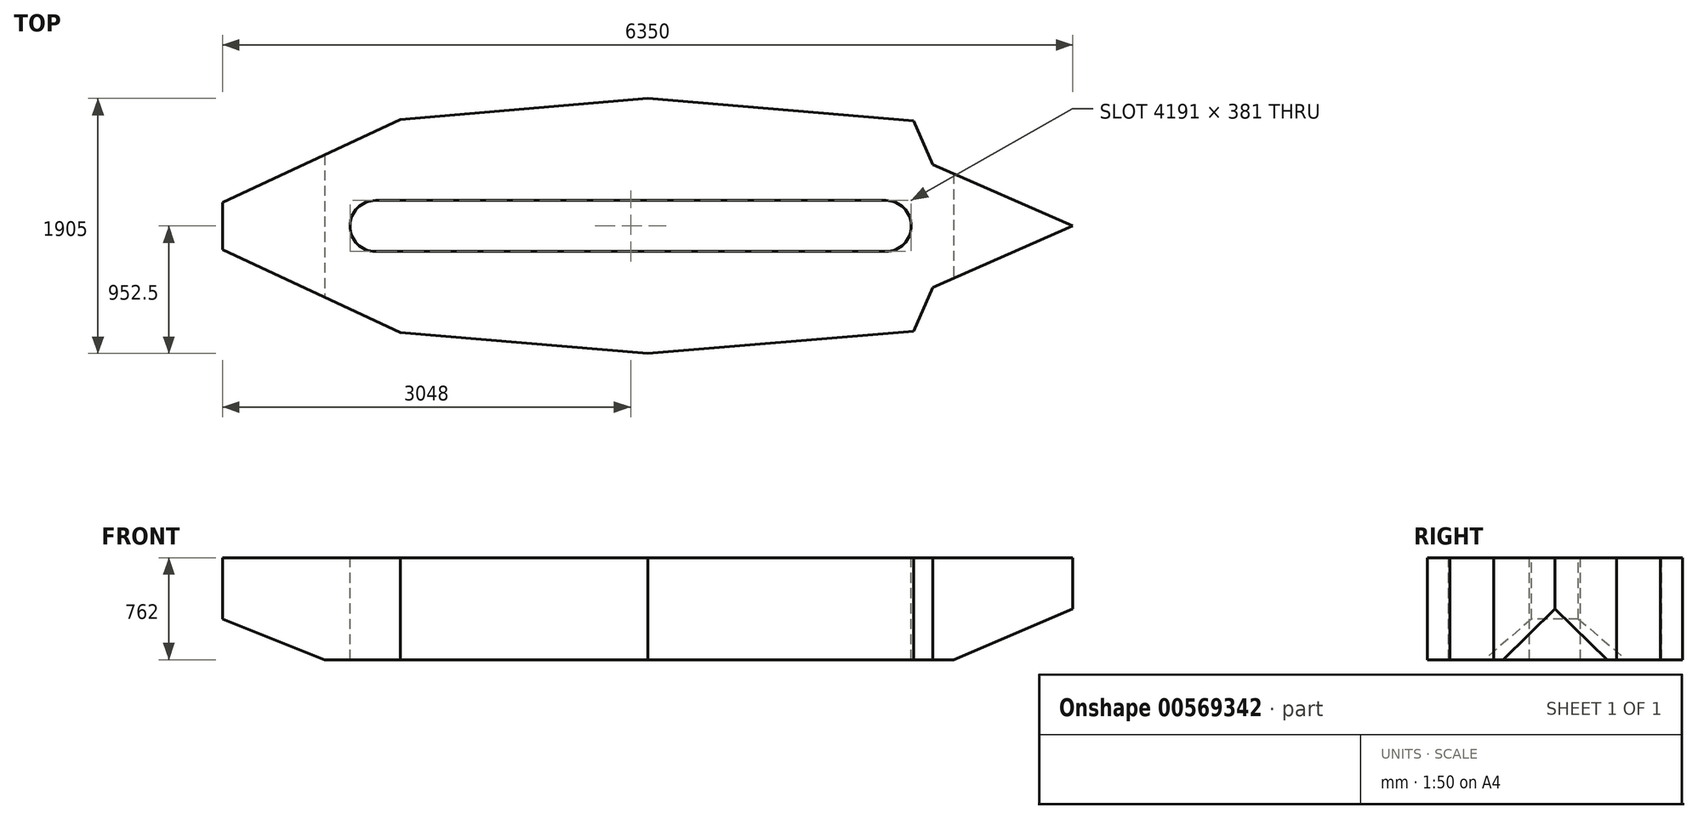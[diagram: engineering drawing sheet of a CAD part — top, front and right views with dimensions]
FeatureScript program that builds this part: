
annotation { "Feature Type Name" : "Feature", "Feature Type Description" : "" }
export const myFeature = defineFeature(function(context is Context, id is Id, definition is map)
    precondition{}
    {
        {
            var Q0;
            Q0=qCreatedBy(makeId("Top.planeOp"),FACE);
            var sketch = newSketch(context, id + "F0", { "sketchPlane" : qUnion([Q0])});
            skLineSegment(sketch, "E0", {"start": v(3175, 0) * mm, "end": v(-3175, 0) * mm, "construction": true});
            skLineSegment(sketch, "E1", {"start": v(0, 952.5) * mm, "end": v(0, -952.5) * mm, "construction": true});
            skLineSegment(sketch, "E2", {"start": v(3175, 0) * mm, "end": v(2128.05, 458.64) * mm});
            skLineSegment(sketch, "E3", {"start": v(2128.05, 458.64) * mm, "end": v(1985.12, 786.19) * mm});
            skLineSegment(sketch, "E4", {"start": v(1985.12, 786.19) * mm, "end": v(0, 952.5) * mm});
            skLineSegment(sketch, "E5", {"start": v(0, 952.5) * mm, "end": v(-1846.34, 794.7) * mm});
            skLineSegment(sketch, "E6", {"start": v(-1846.34, 794.7) * mm, "end": v(-3175, 175.2) * mm});
            skLineSegment(sketch, "E7", {"start": v(-3175, 175.2) * mm, "end": v(-3175, 0) * mm});
            skArc(sketch, "E8", {"start": v(-2032, 190.5) * mm, "mid": v(-2166.7, 134.7) * mm, "end": v(-2222.5, 0) * mm});
            skArc(sketch, "E9", {"start": v(1968.5, 0) * mm, "mid": v(1912.7, 134.7) * mm, "end": v(1778, 190.5) * mm});
            skLineSegment(sketch, "E10", {"start": v(-2032, 190.5) * mm, "end": v(1778, 190.5) * mm});
            skLineSegment(sketch, "E11", {"start": v(-2222.5, 0) * mm, "end": v(-3175, 0) * mm});
            skLineSegment(sketch, "E12", {"start": v(1968.5, 0) * mm, "end": v(3175, 0) * mm});
            skSolve(sketch);
        }
        {
            var Q0;
            Q0=makeQuery(id+"F0.imprint","IMPRINT",FACE,{"disambiguationData":[TD([[makeQuery(id+"F0.imprint","IMPRINT",EDGE,{"derivedFrom":sQuery(id+"F0.wireOp",EDGE,"E2")}),1.0]])]});
            extrude(context, id + "F1", {"entities" : qUnion([Q0]), "oppositeDirection" : true, "depth" : 762 * mm, "offsetDistance" : 25.4 * mm});
        }
        {
            var Q0;
            Q0=makeQuery(id+"F1.opExtrude","SWEPT_FACE",FACE,{"disambiguationData":[OSD([sQuery(id+"F0.wireOp",EDGE,"E11")])]});
            var sketch = newSketch(context, id + "F2", { "sketchPlane" : qUnion([Q0])});
            skLineSegment(sketch, "E13", {"start": v(3175, -381) * mm, "end": v(2286, -762) * mm});
            skLineSegment(sketch, "E14", {"start": v(2286, -762) * mm, "end": v(-2413, -762) * mm});
            skLineSegment(sketch, "E15", {"start": v(-2413, -762) * mm, "end": v(-3175, -457.2) * mm});
            skLineSegment(sketch, "E16", {"start": v(-3175, -457.2) * mm, "end": v(-3175, 0) * mm});
            skLineSegment(sketch, "E17", {"start": v(-3175, 0) * mm, "end": v(3175, 0) * mm});
            skLineSegment(sketch, "E18", {"start": v(3175, 0) * mm, "end": v(3175, -381) * mm});
            skSolve(sketch);
        }
        {
            var Q0;
            Q0 = qSketchRegion(id + "F2", true);
            extrude(context, id + "F3", {"entities" : qUnion([Q0]), "operationType" : NewBodyOperationType.INTERSECT, "endBound" : BoundingType.THROUGH_ALL, "oppositeDirection" : true, "depth" : 25.4 * mm, "offsetDistance" : 25.4 * mm});
        }
        {
            var Q0;
            Q0=makeQuery(id+"F1.opExtrude","SWEPT_BODY",BODY,{"disambiguationData":[OSD([sQuery(id+"F0.wireOp",EDGE,"E2"),sQuery(id+"F0.wireOp",EDGE,"E3"),sQuery(id+"F0.wireOp",EDGE,"E4"),sQuery(id+"F0.wireOp",EDGE,"E5"),sQuery(id+"F0.wireOp",EDGE,"E6"),sQuery(id+"F0.wireOp",EDGE,"E7"),sQuery(id+"F0.wireOp",EDGE,"E8"),sQuery(id+"F0.wireOp",EDGE,"E9"),sQuery(id+"F0.wireOp",EDGE,"E10"),sQuery(id+"F0.wireOp",EDGE,"E11"),sQuery(id+"F0.wireOp",EDGE,"E12")])]});
            var Q1;
            Q1=makeQuery(id+"F1.opExtrude","SWEPT_FACE",FACE,{"disambiguationData":[OSD([sQuery(id+"F0.wireOp",EDGE,"E11")])]});
            mirror(context, id + "F4", {"operationType" : NewBodyOperationType.ADD, "entities" : qUnion([Q0]), "mirrorPlane" : qUnion([Q1])});
        }
    });
